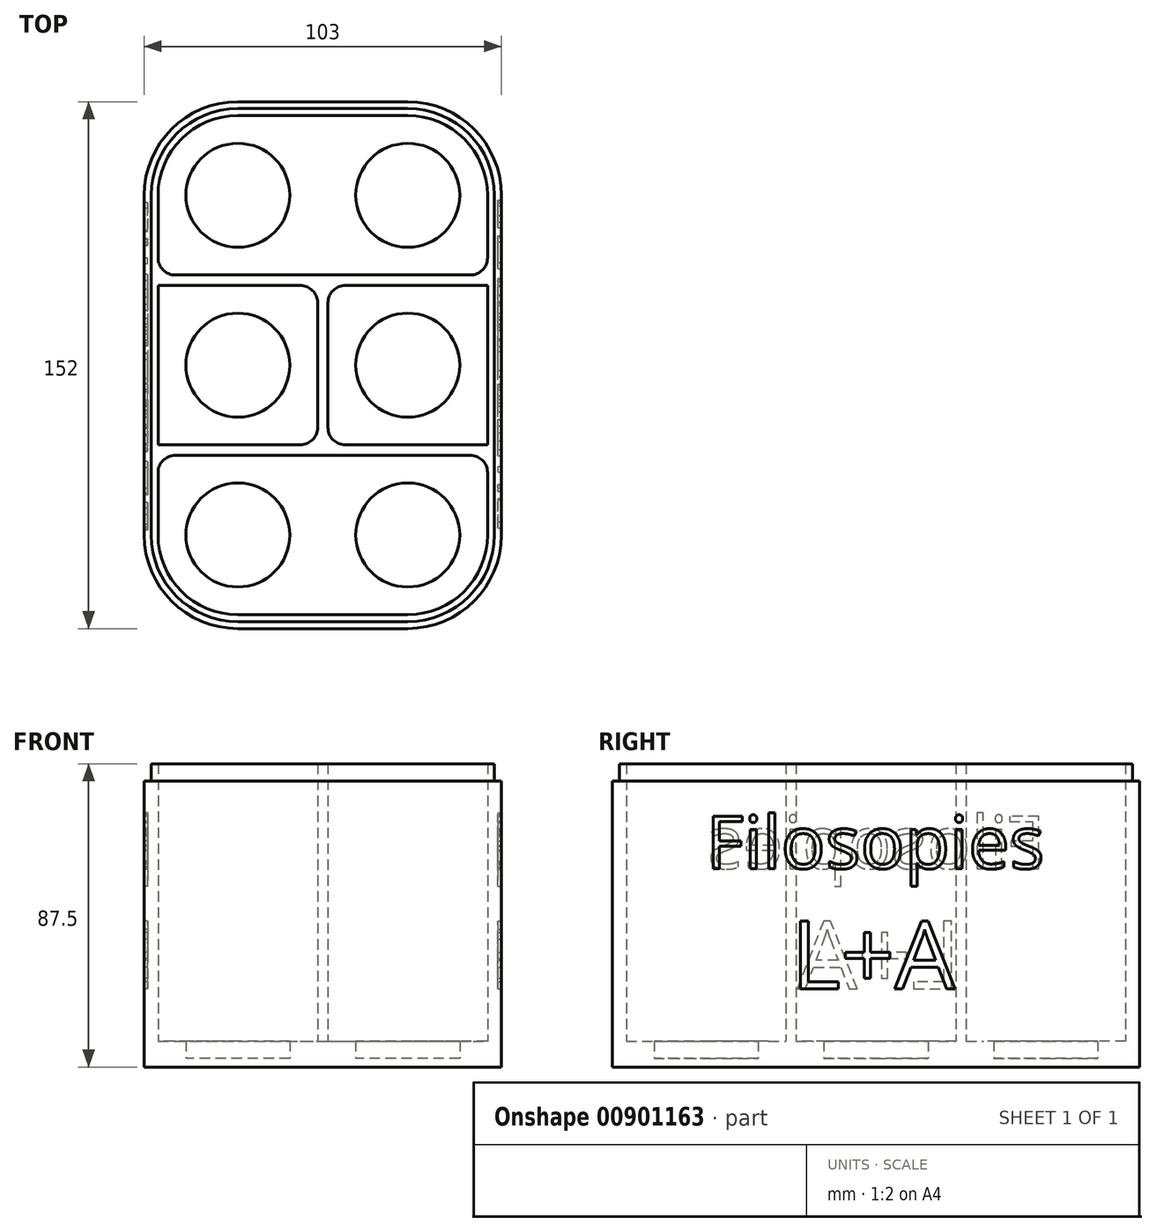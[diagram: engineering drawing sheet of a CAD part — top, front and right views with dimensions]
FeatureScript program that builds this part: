
annotation { "Feature Type Name" : "Feature", "Feature Type Description" : "" }
export const myFeature = defineFeature(function(context is Context, id is Id, definition is map)
    precondition{}
    {
        {
            assignVariable(context, id + "F0", {"name" : "StackedHeight", "anyValue" : 80});
        }
        {
            assignVariable(context, id + "F1", {"name" : "Space", "anyValue" : 5});
        }
        {
            var Q0;
            Q0=qCreatedBy(makeId("Top.planeOp"),FACE);
            var sketch = newSketch(context, id + "F2", { "sketchPlane" : qUnion([Q0])});
            skLineSegment(sketch, "E0.bottom", {"start": v(0, 152) * mm, "end": v(103, 152) * mm});
            skLineSegment(sketch, "E0.top", {"start": v(0, 0) * mm, "end": v(103, 0) * mm});
            skLineSegment(sketch, "E0.left", {"start": v(0, 152) * mm, "end": v(0, 0) * mm});
            skLineSegment(sketch, "E0.right", {"start": v(103, 152) * mm, "end": v(103, 0) * mm});
            skArc(sketch, "E1", {"start": v(27, 152) * mm, "mid": v(7.9, 144.1) * mm, "end": v(0, 125) * mm});
            skArc(sketch, "E2", {"start": v(103, 125) * mm, "mid": v(95.1, 144.1) * mm, "end": v(76, 152) * mm});
            skArc(sketch, "E3", {"start": v(0, 27) * mm, "mid": v(7.9, 7.9) * mm, "end": v(27, 0) * mm});
            skArc(sketch, "E4", {"start": v(76, 0) * mm, "mid": v(95.1, 7.9) * mm, "end": v(103, 27) * mm});
            skSolve(sketch);
        }
        {
            var Q0;
            {var subQ3=sQuery(id+"F2.wireOp",EDGE,"E1");Q0=makeQuery(id+"F2.imprint","IMPRINT",FACE,{"disambiguationData":[TD([[makeQuery(id+"F2.imprint","IMPRINT",EDGE,{"derivedFrom":subQ3}),1.0]])]});}
            extrude(context, id + "F3", {"entities" : qUnion([Q0]), "depth" : (getVariable(context, 'Space') / 2) * mm, "offsetDistance" : 25 * mm});
        }
        {
            var Q0;
            Q0=makeQuery(id+"F3.opExtrude","CAP_FACE",FACE,{"disambiguationData":[OSD([sQuery(id+"F2.wireOp",EDGE,"E0.bottom"),sQuery(id+"F2.wireOp",EDGE,"E0.top"),sQuery(id+"F2.wireOp",EDGE,"E0.left"),sQuery(id+"F2.wireOp",EDGE,"E0.right"),sQuery(id+"F2.wireOp",EDGE,"E1"),sQuery(id+"F2.wireOp",EDGE,"E2"),sQuery(id+"F2.wireOp",EDGE,"E3"),sQuery(id+"F2.wireOp",EDGE,"E4")])],"isStart":false});
            var sketch = newSketch(context, id + "F4", { "sketchPlane" : qUnion([Q0])});
            skCircle(sketch, "E5", {"center": v(27, 125) * mm, "radius": 15 * mm});
            skCircle(sketch, "E6", {"center": v(76, 125) * mm, "radius": 15 * mm});
            skCircle(sketch, "E7", {"center": v(27, 76) * mm, "radius": 15 * mm});
            skCircle(sketch, "E8", {"center": v(76, 76) * mm, "radius": 15 * mm});
            skCircle(sketch, "E9", {"center": v(27, 27) * mm, "radius": 15 * mm});
            skCircle(sketch, "E10", {"center": v(76, 27) * mm, "radius": 15 * mm});
            skSolve(sketch);
        }
        {
            var Q0;
            Q0=makeQuery(id+"F4.imprint","IMPRINT",FACE,{"disambiguationData":[TD([[makeQuery(id+"F4.imprint","IMPRINT",EDGE,{"derivedFrom":sQuery(id+"F4.wireOp",EDGE,"E5")}),-1.0]])]});
            extrude(context, id + "F5", {"entities" : qUnion([Q0]), "operationType" : NewBodyOperationType.ADD, "depth" : (getVariable(context, 'Space')) * mm, "offsetDistance" : 25 * mm});
        }
        {
            var Q0;
            Q0=makeQuery(id+"F5.opExtrude","CAP_FACE",FACE,{"disambiguationData":[OSD([sQuery(id+"F2.wireOp",EDGE,"E0.bottom"),sQuery(id+"F2.wireOp",EDGE,"E0.top"),sQuery(id+"F2.wireOp",EDGE,"E0.left"),sQuery(id+"F2.wireOp",EDGE,"E0.right"),sQuery(id+"F2.wireOp",EDGE,"E1"),sQuery(id+"F2.wireOp",EDGE,"E2"),sQuery(id+"F2.wireOp",EDGE,"E3"),sQuery(id+"F2.wireOp",EDGE,"E4"),sQuery(id+"F4.wireOp",EDGE,"E5"),sQuery(id+"F4.wireOp",EDGE,"E6"),sQuery(id+"F4.wireOp",EDGE,"E7"),sQuery(id+"F4.wireOp",EDGE,"E8"),sQuery(id+"F4.wireOp",EDGE,"E9"),sQuery(id+"F4.wireOp",EDGE,"E10")])],"isStart":false});
            var sketch = newSketch(context, id + "F6", { "sketchPlane" : qUnion([Q0])});
            skArc(sketch, "E11.0", {"start": v(27, 148) * mm, "mid": v(10.74, 141.26) * mm, "end": v(4, 125) * mm});
            skLineSegment(sketch, "E11.1", {"start": v(4, 125) * mm, "end": v(4, 27) * mm});
            skLineSegment(sketch, "E11.2", {"start": v(27, 148) * mm, "end": v(76, 148) * mm});
            skArc(sketch, "E11.3", {"start": v(4, 27) * mm, "mid": v(10.74, 10.74) * mm, "end": v(27, 4) * mm});
            skArc(sketch, "E11.4", {"start": v(99, 125) * mm, "mid": v(92.26, 141.26) * mm, "end": v(76, 148) * mm});
            skLineSegment(sketch, "E11.5", {"start": v(99, 125) * mm, "end": v(99, 27) * mm});
            skArc(sketch, "E11.6", {"start": v(76, 4) * mm, "mid": v(92.26, 10.74) * mm, "end": v(99, 27) * mm});
            skLineSegment(sketch, "E11.7", {"start": v(27, 4) * mm, "end": v(76, 4) * mm});
            skLineSegment(sketch, "E12.bottom", {"start": v(4, 102) * mm, "end": v(99, 102) * mm});
            skLineSegment(sketch, "E12.top", {"start": v(4, 99) * mm, "end": v(99, 99) * mm});
            skLineSegment(sketch, "E12.left", {"start": v(4, 102) * mm, "end": v(4, 99) * mm});
            skLineSegment(sketch, "E12.right", {"start": v(99, 102) * mm, "end": v(99, 99) * mm});
            skLineSegment(sketch, "E13.bottom", {"start": v(4, 53) * mm, "end": v(99, 53) * mm});
            skLineSegment(sketch, "E13.top", {"start": v(4, 50) * mm, "end": v(99, 50) * mm});
            skLineSegment(sketch, "E13.left", {"start": v(4, 53) * mm, "end": v(4, 50) * mm});
            skLineSegment(sketch, "E13.right", {"start": v(99, 53) * mm, "end": v(99, 50) * mm});
            skLineSegment(sketch, "E14.bottom", {"start": v(50, 148) * mm, "end": v(53, 148) * mm});
            skLineSegment(sketch, "E14.top", {"start": v(50, 4) * mm, "end": v(53, 4) * mm});
            skLineSegment(sketch, "E14.left", {"start": v(50, 148) * mm, "end": v(50, 4) * mm});
            skLineSegment(sketch, "E14.right", {"start": v(53, 148) * mm, "end": v(53, 4) * mm});
            skSolve(sketch);
        }
        {
            var Q0;
            Q0=makeQuery(id+"F6.imprint","IMPRINT",FACE,{"disambiguationData":[TD([[makeQuery(id+"F6.imprint","IMPRINT",EDGE,{"derivedFrom":sQuery(id+"F6.wireOp",EDGE,"E11.0")}),-1.0]])]});
            var Q1;
            Q1=makeQuery(id+"F6.imprint","IMPRINT",FACE,{"disambiguationData":[TD([[makeQuery(id+"F6.imprint","IMPRINT",EDGE,{"derivedFrom":sQuery(id+"F6.wireOp",EDGE,"E12.bottom")}),-1.0]])]});
            var Q2;
            Q2=makeQuery(id+"F6.imprint","IMPRINT",FACE,{"disambiguationData":[TD([[makeQuery(id+"F6.imprint","IMPRINT",EDGE,{"derivedFrom":sQuery(id+"F6.wireOp",EDGE,"E13.bottom")}),-1.0]])]});
            var Q3;
            {var subQ5=sQuery(id+"F6.wireOp",EDGE,"E14.bottom");Q3=makeQuery(id+"F6.imprint","IMPRINT",FACE,{"disambiguationData":[TD([[makeQuery(id+"F6.imprint","IMPRINT",EDGE,{"derivedFrom":subQ5}),-1.0]])]});}
            var Q4;
            {var subQ0=sQuery(id+"F6.wireOp",EDGE,"E14.left");var subQ1=sQuery(id+"F6.wireOp",EDGE,"E12.top");var subQ2=makeQuery(id+"F6.imprint","INTERSECT",VERTEX,{"derivedFrom":[subQ1,subQ0]});Q4=makeQuery(id+"F6.imprint","IMPRINT",FACE,{"disambiguationData":[TD([[makeQuery(id+"F6.imprint","IMPRINT",EDGE,{"disambiguationData":[TD([[subQ2,-1.0]])],"derivedFrom":subQ1}),-1.0]])]});}
            var Q5;
            {var subQ5=sQuery(id+"F6.wireOp",EDGE,"E14.top");Q5=makeQuery(id+"F6.imprint","IMPRINT",FACE,{"disambiguationData":[TD([[makeQuery(id+"F6.imprint","IMPRINT",EDGE,{"derivedFrom":subQ5}),1.0]])]});}
            extrude(context, id + "F7", {"entities" : qUnion([Q0, Q1, Q2, Q3, Q4, Q5]), "operationType" : NewBodyOperationType.ADD, "depth" : (getVariable(context, 'StackedHeight')) * mm, "offsetDistance" : 25 * mm});
        }
        {
            var Q0;
            Q0=makeQuery(id+"F7.opExtrude","CAP_FACE",FACE,{"disambiguationData":[OSD([sQuery(id+"F2.wireOp",EDGE,"E0.bottom"),sQuery(id+"F2.wireOp",EDGE,"E0.top"),sQuery(id+"F2.wireOp",EDGE,"E0.left"),sQuery(id+"F2.wireOp",EDGE,"E0.right"),sQuery(id+"F2.wireOp",EDGE,"E1"),sQuery(id+"F2.wireOp",EDGE,"E2"),sQuery(id+"F2.wireOp",EDGE,"E3"),sQuery(id+"F2.wireOp",EDGE,"E4"),sQuery(id+"F6.wireOp",EDGE,"E11.0"),sQuery(id+"F6.wireOp",EDGE,"E11.1"),sQuery(id+"F6.wireOp",EDGE,"E11.2"),sQuery(id+"F6.wireOp",EDGE,"E11.3"),sQuery(id+"F6.wireOp",EDGE,"E11.4"),sQuery(id+"F6.wireOp",EDGE,"E11.5"),sQuery(id+"F6.wireOp",EDGE,"E11.6"),sQuery(id+"F6.wireOp",EDGE,"E11.7"),sQuery(id+"F6.wireOp",EDGE,"E12.bottom"),sQuery(id+"F6.wireOp",EDGE,"E12.top"),sQuery(id+"F6.wireOp",EDGE,"E13.bottom"),sQuery(id+"F6.wireOp",EDGE,"E13.top"),sQuery(id+"F6.wireOp",EDGE,"E14.left"),sQuery(id+"F6.wireOp",EDGE,"E14.right")])],"isStart":false});
            var sketch = newSketch(context, id + "F8", { "sketchPlane" : qUnion([Q0])});
            skArc(sketch, "E15.0", {"start": v(27, 150) * mm, "mid": v(9.32, 142.68) * mm, "end": v(2, 125) * mm});
            skLineSegment(sketch, "E15.1", {"start": v(2, 125) * mm, "end": v(2, 27) * mm});
            skLineSegment(sketch, "E15.2", {"start": v(27, 150) * mm, "end": v(76, 150) * mm});
            skArc(sketch, "E15.3", {"start": v(2, 27) * mm, "mid": v(9.32, 9.32) * mm, "end": v(27, 2) * mm});
            skArc(sketch, "E15.4", {"start": v(101, 125) * mm, "mid": v(93.68, 142.68) * mm, "end": v(76, 150) * mm});
            skLineSegment(sketch, "E15.5", {"start": v(101, 125) * mm, "end": v(101, 27) * mm});
            skArc(sketch, "E15.6", {"start": v(76, 2) * mm, "mid": v(93.68, 9.32) * mm, "end": v(101, 27) * mm});
            skLineSegment(sketch, "E15.7", {"start": v(27, 2) * mm, "end": v(76, 2) * mm});
            skSolve(sketch);
        }
        {
            var Q0;
            Q0=makeQuery(id+"F8.imprint","IMPRINT",FACE,{"disambiguationData":[TD([[makeQuery(id+"F8.imprint","IMPRINT",EDGE,{"derivedFrom":sQuery(id+"F8.wireOp",EDGE,"E15.0")}),-1.0]])]});
            extrude(context, id + "F9", {"entities" : qUnion([Q0]), "operationType" : NewBodyOperationType.REMOVE, "oppositeDirection" : true, "depth" : (getVariable(context, 'Space')) * mm, "offsetDistance" : 25 * mm});
        }
        {
            var Q0;
            Q0=makeQuery(id+"F7.opExtrude","SWEPT_EDGE",EDGE,{"disambiguationData":[OSD([sQuery(id+"F6.wireOp",EDGE,"E13.top"),sQuery(id+"F6.wireOp",EDGE,"E14.right")])]});
            var Q1;
            Q1=makeQuery(id+"F7.opExtrude","SWEPT_EDGE",EDGE,{"disambiguationData":[OSD([sQuery(id+"F6.wireOp",EDGE,"E13.top"),sQuery(id+"F6.wireOp",EDGE,"E14.left")])]});
            var Q2;
            Q2=makeQuery(id+"F7.opExtrude","SWEPT_EDGE",EDGE,{"disambiguationData":[OSD([sQuery(id+"F6.wireOp",EDGE,"E13.bottom"),sQuery(id+"F6.wireOp",EDGE,"E14.right")])]});
            var Q3;
            Q3=makeQuery(id+"F7.opExtrude","SWEPT_EDGE",EDGE,{"disambiguationData":[OSD([sQuery(id+"F6.wireOp",EDGE,"E13.bottom"),sQuery(id+"F6.wireOp",EDGE,"E14.left")])]});
            var Q4;
            Q4=makeQuery(id+"F7.opExtrude","SWEPT_EDGE",EDGE,{"disambiguationData":[OSD([sQuery(id+"F6.wireOp",EDGE,"E12.bottom"),sQuery(id+"F6.wireOp",EDGE,"E14.left")])]});
            var Q5;
            Q5=makeQuery(id+"F7.opExtrude","SWEPT_EDGE",EDGE,{"disambiguationData":[OSD([sQuery(id+"F6.wireOp",EDGE,"E12.bottom"),sQuery(id+"F6.wireOp",EDGE,"E14.right")])]});
            var Q6;
            Q6=makeQuery(id+"F7.opExtrude","SWEPT_EDGE",EDGE,{"disambiguationData":[OSD([sQuery(id+"F6.wireOp",EDGE,"E12.top"),sQuery(id+"F6.wireOp",EDGE,"E14.right")])]});
            var Q7;
            Q7=makeQuery(id+"F7.opExtrude","SWEPT_EDGE",EDGE,{"disambiguationData":[OSD([sQuery(id+"F6.wireOp",EDGE,"E12.top"),sQuery(id+"F6.wireOp",EDGE,"E14.left")])]});
            var Q8;
            Q8=makeQuery(id+"F7.opExtrude","SWEPT_EDGE",EDGE,{"disambiguationData":[OSD([sQuery(id+"F6.wireOp",EDGE,"E11.2"),sQuery(id+"F6.wireOp",EDGE,"E14.bottom"),sQuery(id+"F6.wireOp",EDGE,"E14.left")])]});
            var Q9;
            Q9=makeQuery(id+"F7.opExtrude","SWEPT_EDGE",EDGE,{"disambiguationData":[OSD([sQuery(id+"F6.wireOp",EDGE,"E11.2"),sQuery(id+"F6.wireOp",EDGE,"E14.bottom"),sQuery(id+"F6.wireOp",EDGE,"E14.right")])]});
            var Q10;
            Q10=makeQuery(id+"F7.opExtrude","SWEPT_EDGE",EDGE,{"disambiguationData":[OSD([sQuery(id+"F6.wireOp",EDGE,"E11.7"),sQuery(id+"F6.wireOp",EDGE,"E14.top"),sQuery(id+"F6.wireOp",EDGE,"E14.left")])]});
            var Q11;
            Q11=makeQuery(id+"F7.opExtrude","SWEPT_EDGE",EDGE,{"disambiguationData":[OSD([sQuery(id+"F6.wireOp",EDGE,"E11.7"),sQuery(id+"F6.wireOp",EDGE,"E14.top"),sQuery(id+"F6.wireOp",EDGE,"E14.right")])]});
            fillet(context, id + "F10", {"entities" : qUnion([Q0, Q1, Q2, Q3, Q4, Q5, Q6, Q7, Q8, Q9, Q10, Q11]), "radius" : (getVariable(context, 'Space')) * mm, "tangentPropagation" : true, "allowEdgeOverflow" : false});
        }
        {
            var Q0;
            {var subQ0=sQuery(id+"F2.wireOp",EDGE,"E0.right");Q0=makeQuery(id+"F7.boolean.opBoolean","MERGE",FACE,{"derivedFrom":[makeQuery(id+"F5.boolean.opBoolean","MERGE",FACE,{"derivedFrom":[makeQuery(id+"F3.opExtrude","SWEPT_FACE",FACE,{"disambiguationData":[OSD([subQ0])]}),makeQuery(id+"F5.opExtrude","SWEPT_FACE",FACE,{"disambiguationData":[OSD([subQ0])]})]}),makeQuery(id+"F7.opExtrude","SWEPT_FACE",FACE,{"disambiguationData":[OSD([subQ0])]})]});}
            var sketch = newSketch(context, id + "F11", { "sketchPlane" : qUnion([Q0])});
            skText(sketch, "E16", { "text": "Filosopies", "fontName": "OpenSans-Regular.ttf"});
            skText(sketch, "E17", { "text": "L+A", "fontName": "OpenSans-Regular.ttf"});
            const initialGuessF11  = {"E16": [0.027, 0.05726, 1, 0, 0.01524], "E17": [0.0515, 0.02253, 1, 0, 0.01973]};
            skSetInitialGuess(sketch, initialGuessF11);
            skSolve(sketch);
        }
        {
            var Q0;
            Q0 = qSketchRegion(id + "F11", true);
            extrude(context, id + "F12", {"entities" : qUnion([Q0]), "operationType" : NewBodyOperationType.REMOVE, "oppositeDirection" : true, "depth" : 1 * mm, "offsetDistance" : 25 * mm});
        }
        {
            var Q0;
            {var subQ0=sQuery(id+"F2.wireOp",EDGE,"E0.left");Q0=makeQuery(id+"F7.boolean.opBoolean","MERGE",FACE,{"derivedFrom":[makeQuery(id+"F5.boolean.opBoolean","MERGE",FACE,{"derivedFrom":[makeQuery(id+"F3.opExtrude","SWEPT_FACE",FACE,{"disambiguationData":[OSD([subQ0])]}),makeQuery(id+"F5.opExtrude","SWEPT_FACE",FACE,{"disambiguationData":[OSD([subQ0])]})]}),makeQuery(id+"F7.opExtrude","SWEPT_FACE",FACE,{"disambiguationData":[OSD([subQ0])]})]});}
            var sketch = newSketch(context, id + "F13", { "sketchPlane" : qUnion([Q0])});
            skText(sketch, "E18", { "text": "Filosopies", "fontName": "OpenSans-Regular.ttf"});
            skText(sketch, "E19", { "text": "L+A", "fontName": "OpenSans-Regular.ttf"});
            const initialGuessF13  = {"E18": [-0.125, 0.05726, 1, 0, 0.01524], "E19": [-0.1005, 0.02253, 1, 0, 0.01973]};
            skSetInitialGuess(sketch, initialGuessF13);
            skSolve(sketch);
        }
        {
            var Q0;
            Q0 = qSketchRegion(id + "F13", true);
            extrude(context, id + "F14", {"entities" : qUnion([Q0]), "operationType" : NewBodyOperationType.REMOVE, "oppositeDirection" : true, "depth" : 1 * mm, "offsetDistance" : 25 * mm});
        }
    });
